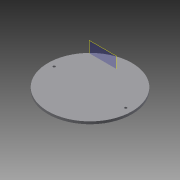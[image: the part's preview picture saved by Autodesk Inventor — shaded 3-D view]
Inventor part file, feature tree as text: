
AUTODESK INVENTOR PART (.ipt)
format: ipt  version: 2014 (Build 180170000, 170)  size: 184,320 bytes
history: native  units: mm
features: reference x20, sketch x5, extrude x4, chamfer x2, plane x1, fillet x1, projected_geometry x1
ambient origin geometry x8: Origin, YZ Plane, XZ Plane, XY Plane, X Axis, Y Axis, Z Axis, Center Point
bodies: Solid1 (feature_tree)
feature tree (34):
  extrude  "Extrusion1"  Depth=58.0mm
  extrude  "Extrusion2"  Depth=2.0mm
  extrude  "Extrusion3"  Depth=8.0mm TaperAngle=0.0deg
  chamfer  "Chamfer1"  Distance=2.0mm Angle=45.0deg
  sketch  "Sketch4"  dims[d14=24.0mm d15=0.0mm d16=8.0mm d17=2.0mm d18=45.0deg]
  plane  "Work Plane1"
  extrude  "Extrusion5"  Depth=8.0mm TaperAngle=45.0deg
  chamfer  "Chamfer2"  [1 undecoded]
  fillet  "Fillet1"  [1 undecoded]
  sketch  "Sketch1"  dims[d0=2.0mm d1=0.0mm d2=58.0mm]
  reference  "Reference1"
  sketch  "Sketch2"  dims[d3=2.0mm d4=2.0mm]
  sketch  "Sketch3"  dims[d5=2.0mm d6=0.0mm d7=8.0mm d8=0.0mm d9=2.0mm d10=2.0mm d11=45.0deg]
  reference  "Reference2"
  reference  "Reference3"
  reference  "Reference4"
  reference  "Reference5"
  reference  "Reference6"
  reference  "Reference7"
  reference  "Reference8"
  reference  "Reference9"
  reference  "Reference10"
  reference  "Reference11"
  reference  "Reference12"
  reference  "Reference13"
  reference  "Reference14"
  reference  "Reference15"
  projected_geometry  "Projected Loop1"
  reference  "Reference16"
  reference  "Reference17"
  reference  "Reference18"
  reference  "Reference19"
  reference  "Reference20"
  sketch  "Sketch5"  dims[d19=1.0mm]
note: 2 required parameter values undecoded (feature->parameter linkage not recoverable at this tier; creation-order binding heuristic only, values carry confidence <= 0.55)
